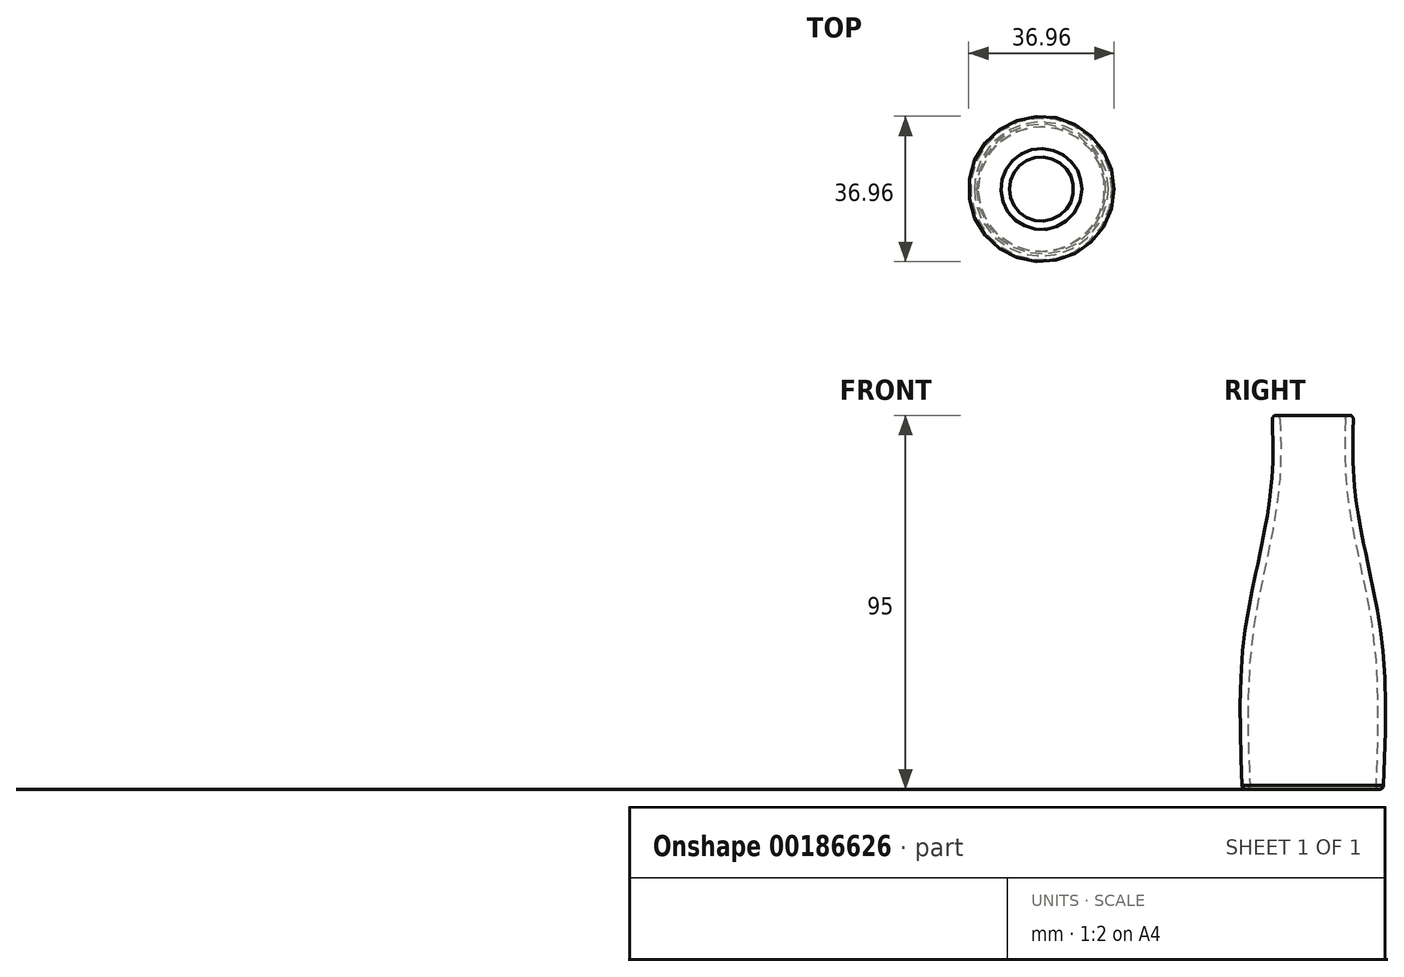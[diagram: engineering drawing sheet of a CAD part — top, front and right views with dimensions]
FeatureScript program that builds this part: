
annotation { "Feature Type Name" : "Feature", "Feature Type Description" : "" }
export const myFeature = defineFeature(function(context is Context, id is Id, definition is map)
    precondition{}
    {
        {
            var Q0;
            Q0=qCreatedBy(makeId("Top.planeOp"),FACE);
            var sketch = newSketch(context, id + "F0", { "sketchPlane" : qUnion([Q0])});
            skCircle(sketch, "E0", {"center": v(0, 0) * mm, "radius": 17.95 * mm});
            skSolve(sketch);
        }
        {
            var Q0;
            Q0=qCreatedBy(makeId("Top.planeOp"),FACE);
            cPlane(context, id + "F1", {"entities" : qUnion([Q0]), "cplaneType" : CPlaneType.OFFSET, "offset" : 40 * mm, "width" : 150 * mm, "height" : 150 * mm});
        }
        {
            var Q0;
            Q0=qCreatedBy(id+"F1.planeOp",FACE);
            var sketch = newSketch(context, id + "F2", { "sketchPlane" : qUnion([Q0])});
            skCircle(sketch, "E1", {"center": v(0, 0) * mm, "radius": 17.25 * mm});
            skSolve(sketch);
        }
        {
            var Q0;
            Q0=qCreatedBy(id+"F1.planeOp",FACE);
            cPlane(context, id + "F3", {"entities" : qUnion([Q0]), "cplaneType" : CPlaneType.OFFSET, "offset" : 40 * mm, "width" : 150 * mm, "height" : 150 * mm});
        }
        {
            var Q0;
            Q0=qCreatedBy(id+"F3.planeOp",FACE);
            var sketch = newSketch(context, id + "F4", { "sketchPlane" : qUnion([Q0])});
            skCircle(sketch, "E2", {"center": v(0, 0) * mm, "radius": 10.32 * mm});
            skSolve(sketch);
        }
        {
            var Q0;
            Q0=qCreatedBy(id+"F3.planeOp",FACE);
            cPlane(context, id + "F5", {"entities" : qUnion([Q0]), "cplaneType" : CPlaneType.OFFSET, "offset" : 15 * mm, "width" : 150 * mm, "height" : 150 * mm});
        }
        {
            var Q0;
            Q0=qCreatedBy(id+"F5.planeOp",FACE);
            var sketch = newSketch(context, id + "F6", { "sketchPlane" : qUnion([Q0])});
            skCircle(sketch, "E3", {"center": v(0, 0) * mm, "radius": 10.32 * mm});
            skSolve(sketch);
        }
        {
            var Q0;
            Q0=makeQuery(id+"F0.imprint","IMPRINT",FACE,{"disambiguationData":[TD([[makeQuery(id+"F0.imprint","IMPRINT",EDGE,{"derivedFrom":sQuery(id+"F0.wireOp",EDGE,"E0")}),1.0]])]});
            var Q1;
            Q1=makeQuery(id+"F2.imprint","IMPRINT",FACE,{"disambiguationData":[TD([[makeQuery(id+"F2.imprint","IMPRINT",EDGE,{"derivedFrom":sQuery(id+"F2.wireOp",EDGE,"E1")}),1.0]])]});
            var Q2;
            Q2=makeQuery(id+"F4.imprint","IMPRINT",FACE,{"disambiguationData":[TD([[makeQuery(id+"F4.imprint","IMPRINT",EDGE,{"derivedFrom":sQuery(id+"F4.wireOp",EDGE,"E2")}),1.0]])]});
            var Q3;
            Q3=makeQuery(id+"F6.imprint","IMPRINT",FACE,{"disambiguationData":[TD([[makeQuery(id+"F6.imprint","IMPRINT",EDGE,{"derivedFrom":sQuery(id+"F6.wireOp",EDGE,"E3")}),1.0]])]});
            loft(context, id + "F7", {"sheetProfilesArray" : [{ "sheetProfileEntities" : qUnion([Q0]) }, { "sheetProfileEntities" : qUnion([Q1]) }, { "sheetProfileEntities" : qUnion([Q2]) }, { "sheetProfileEntities" : qUnion([Q3]) }]});
        }
        {
            var Q0;
            Q0=makeQuery(id+"F7.opLoft","CAP_FACE",FACE,{"disambiguationData":[OSD([makeQuery(id+"F6.imprint","IMPRINT",FACE,{"disambiguationData":[TD([[makeQuery(id+"F6.imprint","IMPRINT",EDGE,{"derivedFrom":sQuery(id+"F6.wireOp",EDGE,"E3")}),1.0]])]})])],"isStart":true});
            var Q1;
            Q1=makeQuery(id+"F7.opLoft","CAP_FACE",FACE,{"disambiguationData":[OSD([makeQuery(id+"F0.imprint","IMPRINT",FACE,{"disambiguationData":[TD([[makeQuery(id+"F0.imprint","IMPRINT",EDGE,{"derivedFrom":sQuery(id+"F0.wireOp",EDGE,"E0")}),1.0]])]})])],"isStart":true});
            shell(context, id + "F8", {"entities" : qUnion([Q0, Q1]), "thickness" : 2 * mm});
        }
        {
            var Q0;
            Q0=makeQuery(id+"F8.opShell","OFFSET_EDGE",EDGE,{"disambiguationData":[OSD([sQuery(id+"F0.wireOp",EDGE,"E0")])]});
            var Q1;
            Q1=makeQuery(id+"F7.opLoft","MID_CAP_EDGE",EDGE,{"disambiguationData":[OSD([sQuery(id+"F0.wireOp",EDGE,"E0")])],"capPos":0.0});
            var Q2;
            Q2=makeQuery(id+"F8.opShell","OFFSET_EDGE",EDGE,{"disambiguationData":[OSD([sQuery(id+"F0.wireOp",EDGE,"E0"),sQuery(id+"F6.wireOp",EDGE,"E3")])]});
            var Q3;
            Q3=makeQuery(id+"F7.opLoft","MID_CAP_EDGE",EDGE,{"disambiguationData":[OSD([sQuery(id+"F0.wireOp",EDGE,"E0"),sQuery(id+"F6.wireOp",EDGE,"E3")])],"capPos":3.0});
            fillet(context, id + "F9", {"entities" : qUnion([Q0, Q1, Q2, Q3]), "radius" : 1 * mm, "tangentPropagation" : true, "allowEdgeOverflow" : false});
        }
    });
